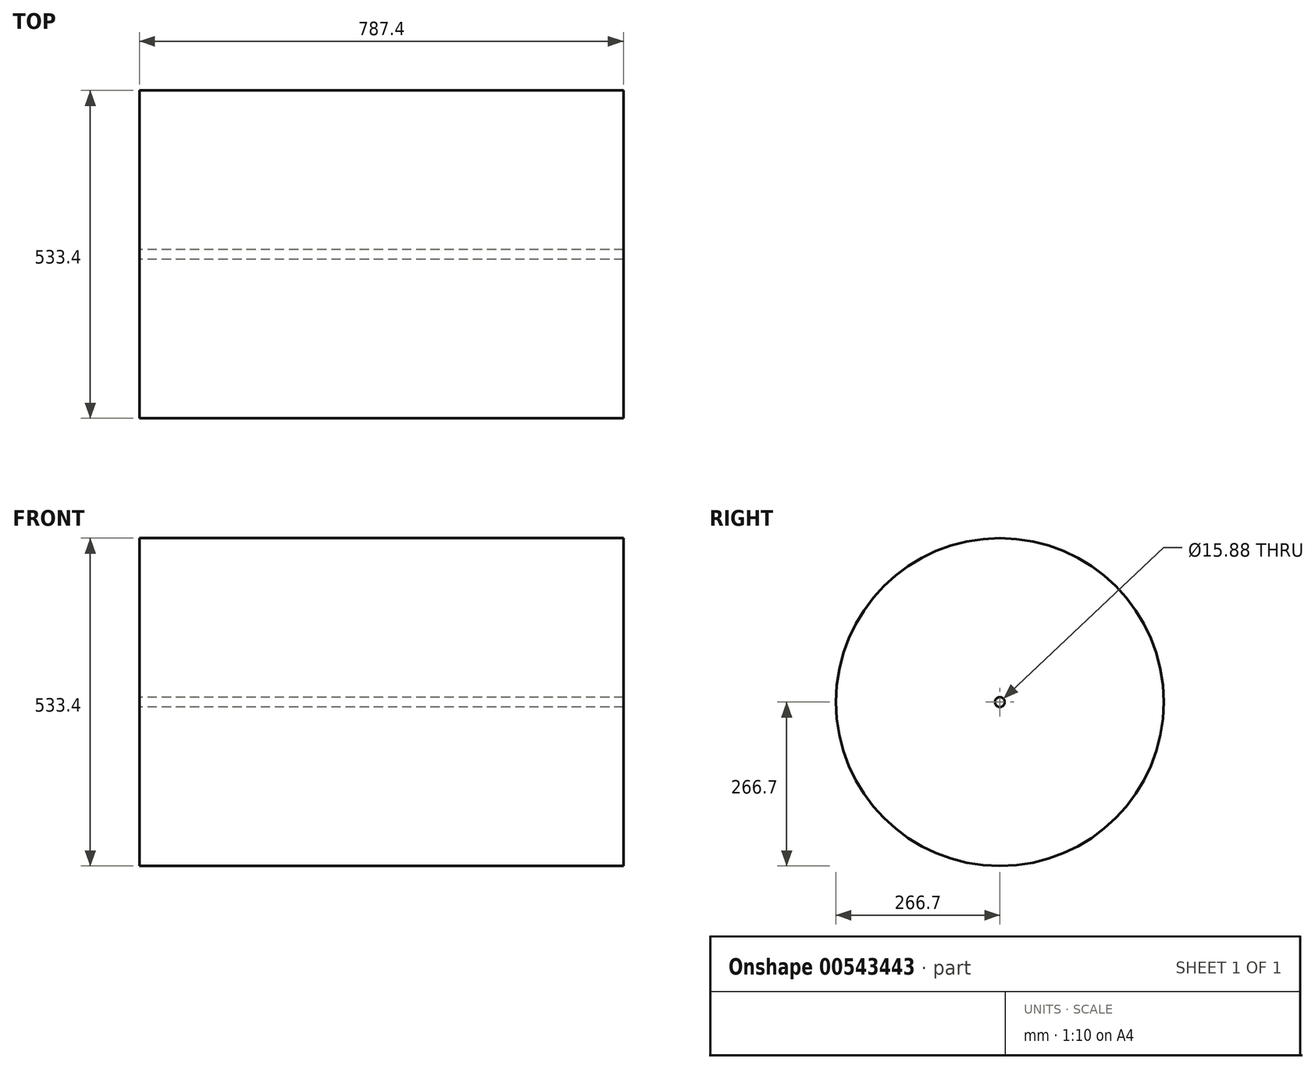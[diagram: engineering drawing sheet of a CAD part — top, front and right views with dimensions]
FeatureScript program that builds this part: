
annotation { "Feature Type Name" : "Feature", "Feature Type Description" : "" }
export const myFeature = defineFeature(function(context is Context, id is Id, definition is map)
    precondition{}
    {
        {
            var Q0;
            Q0=qCreatedBy(makeId("Right.planeOp"),FACE);
            var sketch = newSketch(context, id + "F0", { "sketchPlane" : qUnion([Q0])});
            skCircle(sketch, "E0", {"center": v(0, 0) * mm, "radius": 266.7 * mm});
            skSolve(sketch);
        }
        {
            var Q0;
            Q0=qCreatedBy(makeId("Front.planeOp"),FACE);
            var sketch = newSketch(context, id + "F1", { "sketchPlane" : qUnion([Q0])});
            skSolve(sketch);
        }
        {
            var Q0;
            Q0 = qSketchRegion(id + "F1", true);
            var Q1;
            Q1=makeQuery(id+"F0.imprint","IMPRINT",FACE,{"disambiguationData":[TD([[makeQuery(id+"F0.imprint","IMPRINT",EDGE,{"derivedFrom":sQuery(id+"F0.wireOp",EDGE,"E0")}),1.0]])]});
            extrude(context, id + "F2", {"entities" : qUnion([Q0, Q1]), "depth" : 787.4 * mm, "offsetDistance" : 25.4 * mm});
        }
        {
            var Q0;
            Q0=sQuery(id+"F0.wireOp",VERTEX,"E0.center");
            var Q1;
            Q1=makeQuery(id+"F2.opExtrude","SWEPT_BODY",BODY,{"disambiguationData":[OSD([sQuery(id+"F0.wireOp",EDGE,"E0")])]});
            hole(context, id + "F3", {"style" : HoleStyle.SIMPLE, "endStyle" : HoleEndStyle.THROUGH, "oppositeDirection" : true, "holeDiameter" : 15.88 * mm, "isTappedThrough" : true, "tappedDepth" : 12.7 * mm, "tapClearance" : 3, "locations" : qUnion([Q0]), "scope" : qUnion([Q1])});
        }
    });
